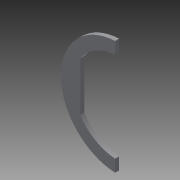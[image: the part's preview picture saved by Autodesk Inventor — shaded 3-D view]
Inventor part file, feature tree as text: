
AUTODESK INVENTOR PART (.ipt)
format: ipt  version: 2015 (Build 190159000, 159)  size: 79,872 bytes
history: native  units: mm
features: extrude x1, sketch x1
ambient origin geometry x8: Origin, YZ Plane, XZ Plane, XY Plane, X Axis, Y Axis, Z Axis, Center Point
bodies: Solid1 (feature_tree)
feature tree (2):
  extrude  "Extrusion1"  Depth=5.0mm
  sketch  "Sketch1"  dims[d1=141.0mm d2=15.0mm d3=15.0mm d7=24.0mm d8=5.0mm d9=0.0mm]
